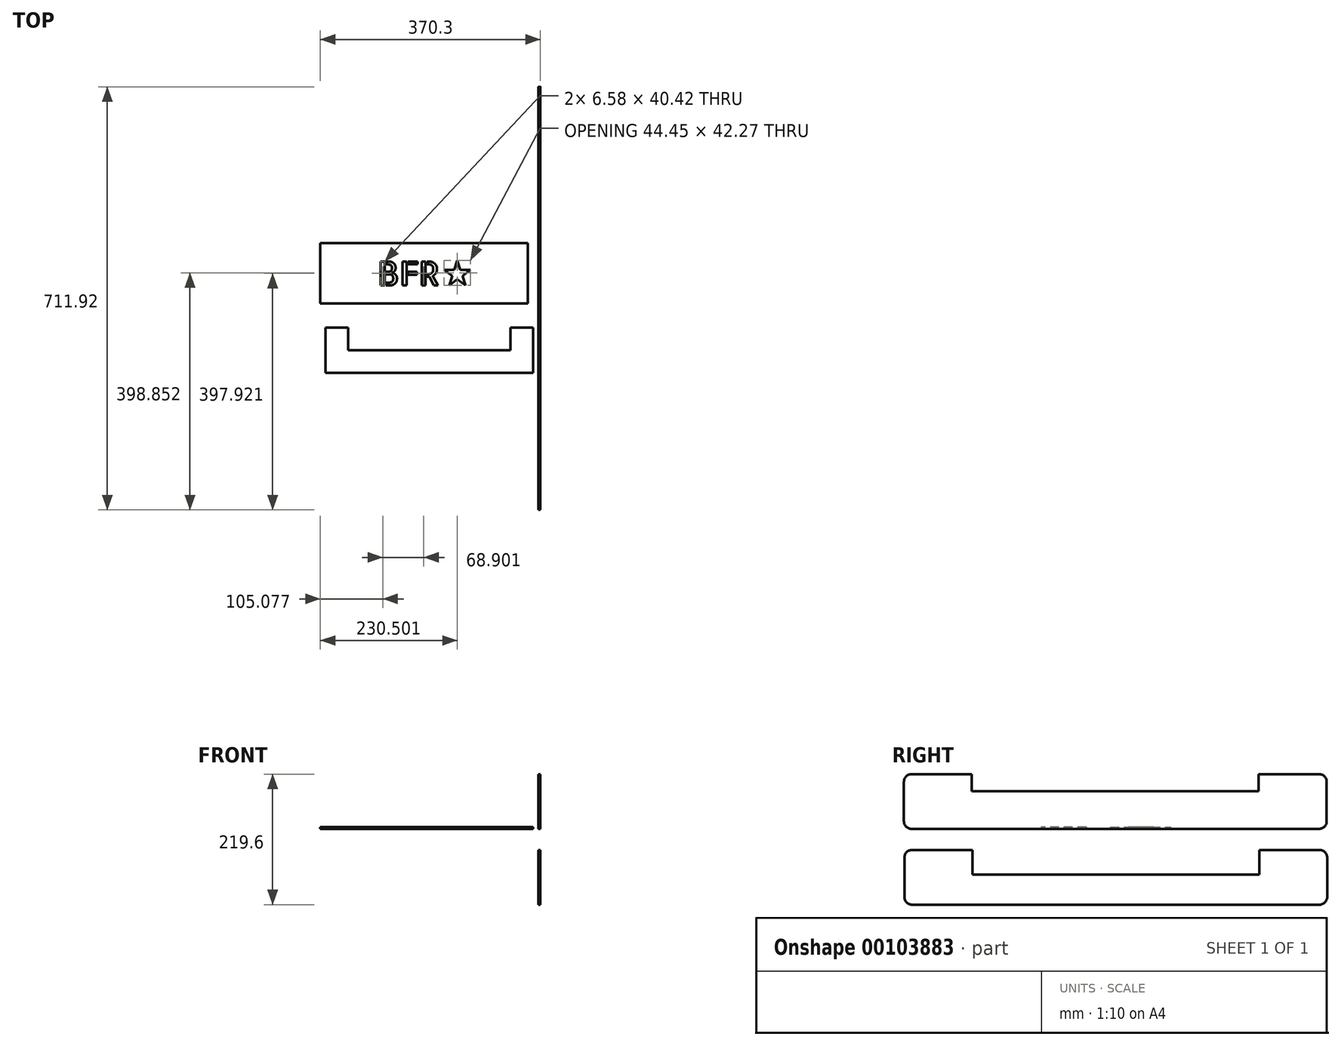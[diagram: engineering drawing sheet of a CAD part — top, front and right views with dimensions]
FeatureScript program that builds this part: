
annotation { "Feature Type Name" : "Feature", "Feature Type Description" : "" }
export const myFeature = defineFeature(function(context is Context, id is Id, definition is map)
    precondition{}
    {
        {
            var Q0;
            Q0=qCreatedBy(makeId("Right.planeOp"),FACE);
            var sketch = newSketch(context, id + "F0", { "sketchPlane" : qUnion([Q0])});
            skLineSegment(sketch, "E0", {"start": v(-176.16, 63.5) * mm, "end": v(306.44, 63.5) * mm});
            skLineSegment(sketch, "E1", {"start": v(306.44, 63.5) * mm, "end": v(306.44, 92.07) * mm});
            skLineSegment(sketch, "E2", {"start": v(306.44, 92.07) * mm, "end": v(408.04, 92.07) * mm});
            skLineSegment(sketch, "E3", {"start": v(420.74, 79.37) * mm, "end": v(420.74, 12.7) * mm});
            skLineSegment(sketch, "E4", {"start": v(408.04, 0) * mm, "end": v(-277.76, 0) * mm});
            skLineSegment(sketch, "E5", {"start": v(-290.46, 12.7) * mm, "end": v(-290.46, 79.37) * mm});
            skLineSegment(sketch, "E6", {"start": v(-277.76, 92.08) * mm, "end": v(-176.16, 92.08) * mm});
            skLineSegment(sketch, "E7", {"start": v(-176.16, 92.07) * mm, "end": v(-176.16, 63.5) * mm});
            skPoint(sketch, "E8.visualSharp", {"position": v(-290.46, 92.08) * mm});
            skArc(sketch, "E8.filletArc", {"start": v(-277.76, 92.07) * mm, "mid": v(-286.74, 88.36) * mm, "end": v(-290.46, 79.37) * mm});
            skPoint(sketch, "E9.visualSharp", {"position": v(420.74, 92.07) * mm});
            skArc(sketch, "E9.filletArc", {"start": v(420.74, 79.37) * mm, "mid": v(417.02, 88.36) * mm, "end": v(408.04, 92.07) * mm});
            skPoint(sketch, "E10.visualSharp", {"position": v(420.74, 0) * mm});
            skArc(sketch, "E10.filletArc", {"start": v(408.04, 0) * mm, "mid": v(417.02, 3.72) * mm, "end": v(420.74, 12.7) * mm});
            skPoint(sketch, "E11.visualSharp", {"position": v(-290.46, 0) * mm});
            skArc(sketch, "E11.filletArc", {"start": v(-290.46, 12.7) * mm, "mid": v(-286.74, 3.72) * mm, "end": v(-277.76, 0) * mm});
            skSolve(sketch);
        }
        {
            var Q0;
            Q0=makeQuery(id+"F0.imprint","IMPRINT",FACE,{"disambiguationData":[TD([[makeQuery(id+"F0.imprint","IMPRINT",EDGE,{"derivedFrom":sQuery(id+"F0.wireOp",EDGE,"E0")}),-1.0]])]});
            extrude(context, id + "F1", {"entities" : qUnion([Q0]), "depth" : 3.17 * mm});
        }
        {
            var Q0;
            Q0=qCreatedBy(makeId("Top.planeOp"),FACE);
            var sketch = newSketch(context, id + "F2", { "sketchPlane" : qUnion([Q0])});
            skLineSegment(sketch, "E12", {"start": v(-9.4, -59.92) * mm, "end": v(-358.64, -59.92) * mm});
            skLineSegment(sketch, "E13", {"start": v(-358.64, -59.92) * mm, "end": v(-358.64, 16.28) * mm});
            skLineSegment(sketch, "E14", {"start": v(-358.64, 16.28) * mm, "end": v(-320.54, 16.28) * mm});
            skLineSegment(sketch, "E15", {"start": v(-320.54, 16.28) * mm, "end": v(-320.54, -21.82) * mm});
            skLineSegment(sketch, "E16", {"start": v(-320.54, -21.82) * mm, "end": v(-47.5, -21.82) * mm});
            skLineSegment(sketch, "E17", {"start": v(-47.5, -21.82) * mm, "end": v(-47.5, 16.28) * mm});
            skLineSegment(sketch, "E18", {"start": v(-47.5, 16.28) * mm, "end": v(-9.4, 16.28) * mm});
            skLineSegment(sketch, "E19", {"start": v(-9.4, 16.28) * mm, "end": v(-9.4, -59.92) * mm});
            skSolve(sketch);
        }
        {
            var Q0;
            Q0=makeQuery(id+"F2.imprint","IMPRINT",FACE,{"disambiguationData":[TD([[makeQuery(id+"F2.imprint","IMPRINT",EDGE,{"derivedFrom":sQuery(id+"F2.wireOp",EDGE,"E12")}),-1.0]])]});
            extrude(context, id + "F3", {"entities" : qUnion([Q0]), "depth" : 3.17 * mm});
        }
        {
            var Q0;
            Q0=qCreatedBy(makeId("Top.planeOp"),FACE);
            var sketch = newSketch(context, id + "F4", { "sketchPlane" : qUnion([Q0])});
            skLineSegment(sketch, "E20.bottom", {"start": v(-367.13, 56.77) * mm, "end": v(-17.88, 56.77) * mm});
            skLineSegment(sketch, "E20.top", {"start": v(-367.13, 158.37) * mm, "end": v(-17.88, 158.37) * mm});
            skLineSegment(sketch, "E20.left", {"start": v(-367.13, 56.77) * mm, "end": v(-367.13, 158.37) * mm});
            skLineSegment(sketch, "E20.right", {"start": v(-17.88, 56.77) * mm, "end": v(-17.88, 158.37) * mm});
            skLineSegment(sketch, "E21", {"start": v(-150.36, 87.25) * mm, "end": v(-136.63, 97.23) * mm});
            skLineSegment(sketch, "E22", {"start": v(-114.4, 113.38) * mm, "end": v(-131.38, 113.38) * mm});
            skLineSegment(sketch, "E23", {"start": v(-158.85, 113.38) * mm, "end": v(-145.12, 103.4) * mm});
            skLineSegment(sketch, "E24", {"start": v(-122.9, 87.25) * mm, "end": v(-128.14, 103.4) * mm});
            skLineSegment(sketch, "E25", {"start": v(-136.63, 129.53) * mm, "end": v(-141.88, 113.38) * mm});
            skText(sketch, "E26", { "text": "BFR", "fontName": "AllertaStencil-Regular.ttf"});
            skLineSegment(sketch, "E27.trimOffspring", {"start": v(-145.12, 103.4) * mm, "end": v(-150.36, 87.25) * mm});
            skLineSegment(sketch, "E28.trimOffspring", {"start": v(-141.88, 113.38) * mm, "end": v(-158.85, 113.38) * mm});
            skLineSegment(sketch, "E29.trimOffspring", {"start": v(-128.14, 103.4) * mm, "end": v(-114.4, 113.38) * mm});
            skLineSegment(sketch, "E30.trimOffspring", {"start": v(-136.63, 97.23) * mm, "end": v(-122.9, 87.25) * mm});
            skLineSegment(sketch, "E31.trimOffspring", {"start": v(-131.38, 113.38) * mm, "end": v(-136.63, 129.53) * mm});
            const initialGuessF4  = {"E26": [-0.27061, 0.08725, 1, 0, 0.04044]};
            skSetInitialGuess(sketch, initialGuessF4);
            skSolve(sketch);
        }
        {
            var Q0;
            Q0=makeQuery(id+"F4.imprint","IMPRINT",FACE,{"disambiguationData":[TD([[makeQuery(id+"F4.imprint","IMPRINT",EDGE,{"derivedFrom":sQuery(id+"F4.wireOp",EDGE,"E20.bottom")}),1.0]])]});
            var Q1;
            Q1 = qConstructionFilter(qBodyType(qCreatedBy(id + "F4" ,EDGE), BodyType.WIRE), ConstructionObject.NO);
            extrude(context, id + "F5", {"entities" : qUnion([Q0]), "surfaceEntities" : qUnion([Q1]), "depth" : 3.17 * mm});
        }
        {
            var Q0;
            Q0=qCreatedBy(makeId("Right.planeOp"),FACE);
            var sketch = newSketch(context, id + "F6", { "sketchPlane" : qUnion([Q0])});
            skLineSegment(sketch, "E32", {"start": v(-175.44, -76.72) * mm, "end": v(307.16, -76.72) * mm});
            skLineSegment(sketch, "E33", {"start": v(307.16, -76.72) * mm, "end": v(307.16, -35.45) * mm});
            skLineSegment(sketch, "E34", {"start": v(307.16, -35.45) * mm, "end": v(408.76, -35.45) * mm});
            skLineSegment(sketch, "E35", {"start": v(421.46, -48.15) * mm, "end": v(421.46, -114.82) * mm});
            skLineSegment(sketch, "E36", {"start": v(408.76, -127.52) * mm, "end": v(-277.04, -127.52) * mm});
            skLineSegment(sketch, "E37", {"start": v(-289.74, -114.82) * mm, "end": v(-289.74, -48.15) * mm});
            skLineSegment(sketch, "E38", {"start": v(-277.04, -35.45) * mm, "end": v(-175.44, -35.45) * mm});
            skLineSegment(sketch, "E39", {"start": v(-175.44, -35.45) * mm, "end": v(-175.44, -76.72) * mm});
            skPoint(sketch, "E40.visualSharp", {"position": v(-289.74, -35.45) * mm});
            skArc(sketch, "E40.filletArc", {"start": v(-277.04, -35.45) * mm, "mid": v(-286.02, -39.17) * mm, "end": v(-289.74, -48.15) * mm});
            skPoint(sketch, "E41.visualSharp", {"position": v(421.46, -35.45) * mm});
            skArc(sketch, "E41.filletArc", {"start": v(421.46, -48.15) * mm, "mid": v(417.74, -39.17) * mm, "end": v(408.76, -35.45) * mm});
            skPoint(sketch, "E42.visualSharp", {"position": v(421.46, -127.52) * mm});
            skArc(sketch, "E42.filletArc", {"start": v(408.76, -127.52) * mm, "mid": v(417.74, -123.8) * mm, "end": v(421.46, -114.82) * mm});
            skPoint(sketch, "E43.visualSharp", {"position": v(-289.74, -127.52) * mm});
            skArc(sketch, "E43.filletArc", {"start": v(-289.74, -114.82) * mm, "mid": v(-286.02, -123.8) * mm, "end": v(-277.04, -127.52) * mm});
            skSolve(sketch);
        }
        {
            var Q0;
            Q0=makeQuery(id+"F6.imprint","IMPRINT",FACE,{"disambiguationData":[TD([[makeQuery(id+"F6.imprint","IMPRINT",EDGE,{"derivedFrom":sQuery(id+"F6.wireOp",EDGE,"E32")}),-1.0]])]});
            extrude(context, id + "F7", {"entities" : qUnion([Q0]), "depth" : 3.17 * mm});
        }
    });
